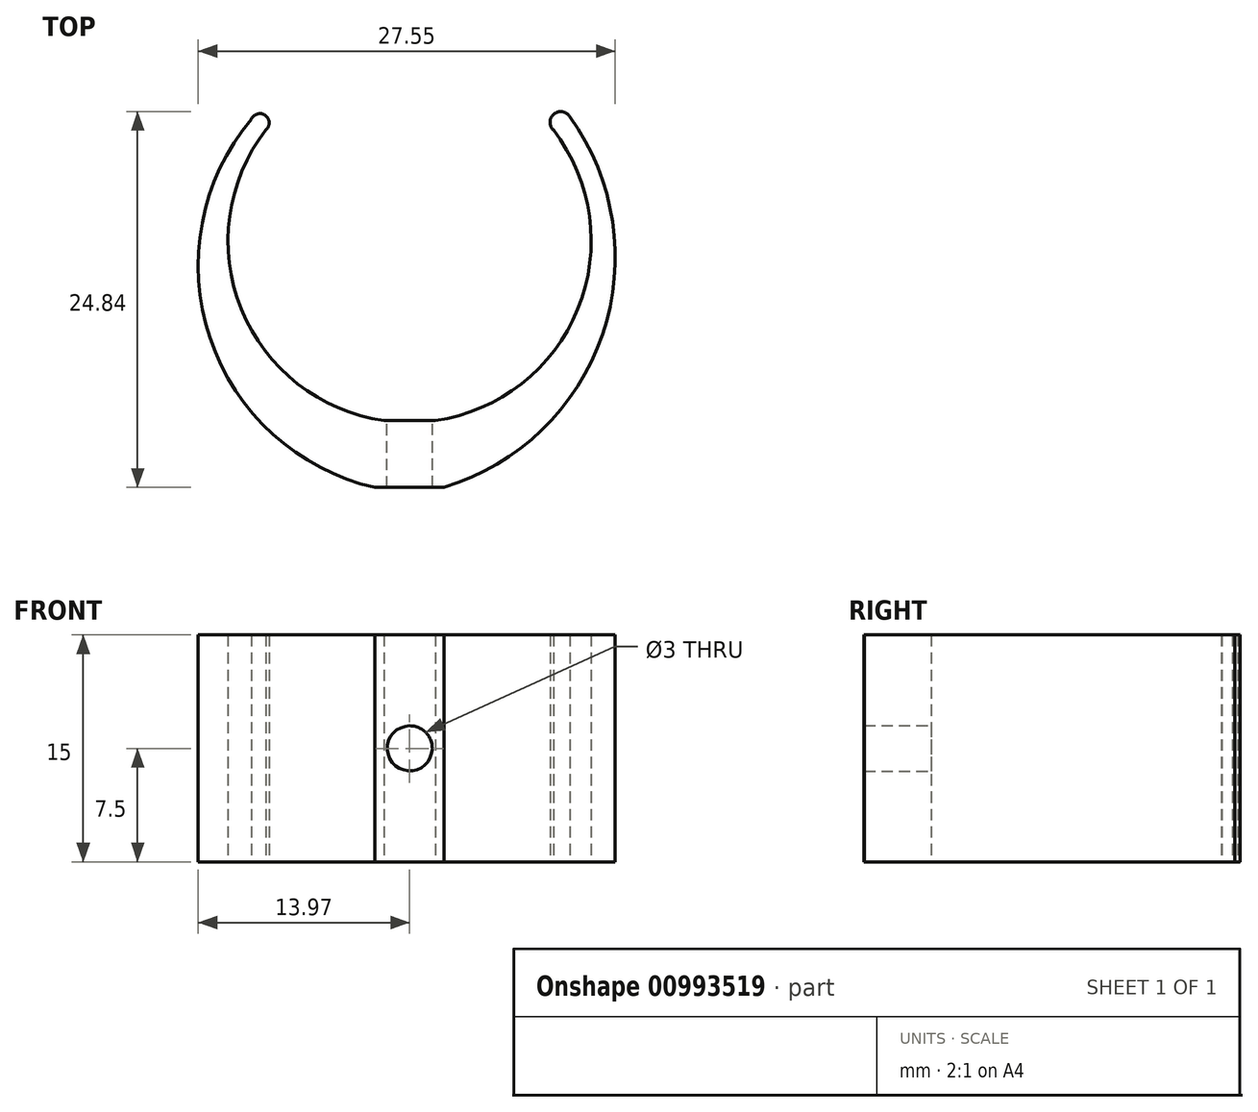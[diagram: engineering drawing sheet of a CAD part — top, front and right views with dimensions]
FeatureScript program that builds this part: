
annotation { "Feature Type Name" : "Feature", "Feature Type Description" : "" }
export const myFeature = defineFeature(function(context is Context, id is Id, definition is map)
    precondition{}
    {
        {
            var Q0;
            Q0=qCreatedBy(makeId("Top.planeOp"),FACE);
            var sketch = newSketch(context, id + "F0", { "sketchPlane" : qUnion([Q0])});
            skPoint(sketch, "E0.middle", {"position": v(0, 0) * mm});
            skLineSegment(sketch, "E1", {"start": v(-1.9, -11.88) * mm, "end": v(1.9, -11.88) * mm});
            skArc(sketch, "E2", {"start": v(-9.5, 7.33) * mm, "mid": v(-11.12, -4.5) * mm, "end": v(-1.7, -11.88) * mm});
            skArc(sketch, "E3", {"start": v(9.5, 7.33) * mm, "mid": v(11.12, -4.51) * mm, "end": v(1.7, -11.88) * mm});
            skArc(sketch, "E4", {"start": v(-10.46, 8.03) * mm, "mid": v(-13.2, -6.42) * mm, "end": v(-2.3, -16.3) * mm});
            skArc(sketch, "E5", {"start": v(2.28, -16.29) * mm, "mid": v(12.74, -6.19) * mm, "end": v(10.58, 8.2) * mm});
            skArc(sketch, "E6", {"start": v(-9.5, 7.33) * mm, "mid": v(-9.54, 8.3) * mm, "end": v(-10.46, 8.03) * mm});
            skArc(sketch, "E7", {"start": v(10.58, 8.2) * mm, "mid": v(9.54, 8.39) * mm, "end": v(9.5, 7.33) * mm});
            skLineSegment(sketch, "E8", {"start": v(-2.3, -16.3) * mm, "end": v(2.28, -16.29) * mm});
            skSolve(sketch);
        }
        {
            var Q0;
            Q0 = qSketchRegion(id + "FSJDVHFnWiuX55M_1", true);
            var Q1;
            {var subQ1=sQuery(id+"F0.wireOp",EDGE,"E2");Q1=makeQuery(id+"F0.imprint","IMPRINT",FACE,{"disambiguationData":[TD([[makeQuery(id+"F0.imprint","IMPRINT",EDGE,{"derivedFrom":subQ1}),-1.0]])]});}
            extrude(context, id + "F1", {"entities" : qUnion([Q0, Q1]), "depth" : 15 * mm, "offsetDistance" : 25 * mm});
        }
        {
            var Q0;
            Q0=makeQuery(id+"F1.opExtrude","SWEPT_FACE",FACE,{"disambiguationData":[OSD([sQuery(id+"F0.wireOp",EDGE,"E1")])]});
            var sketch = newSketch(context, id + "F2", { "sketchPlane" : qUnion([Q0])});
            skCircle(sketch, "E9", {"center": v(0, 7.5) * mm, "radius": 1.5 * mm});
            skPoint(sketch, "E9.centerSnap0", {"position": v(-1.7, 7.5) * mm});
            skSolve(sketch);
        }
        {
            var Q0;
            Q0=makeQuery(id+"F2.imprint","IMPRINT",FACE,{"disambiguationData":[TD([[makeQuery(id+"F2.imprint","IMPRINT",EDGE,{"derivedFrom":sQuery(id+"F2.wireOp",EDGE,"E9")}),1.0]])]});
            extrude(context, id + "F3", {"entities" : qUnion([Q0]), "operationType" : NewBodyOperationType.REMOVE, "endBound" : BoundingType.THROUGH_ALL, "oppositeDirection" : true, "depth" : 25 * mm, "offsetDistance" : 25 * mm});
        }
    });
